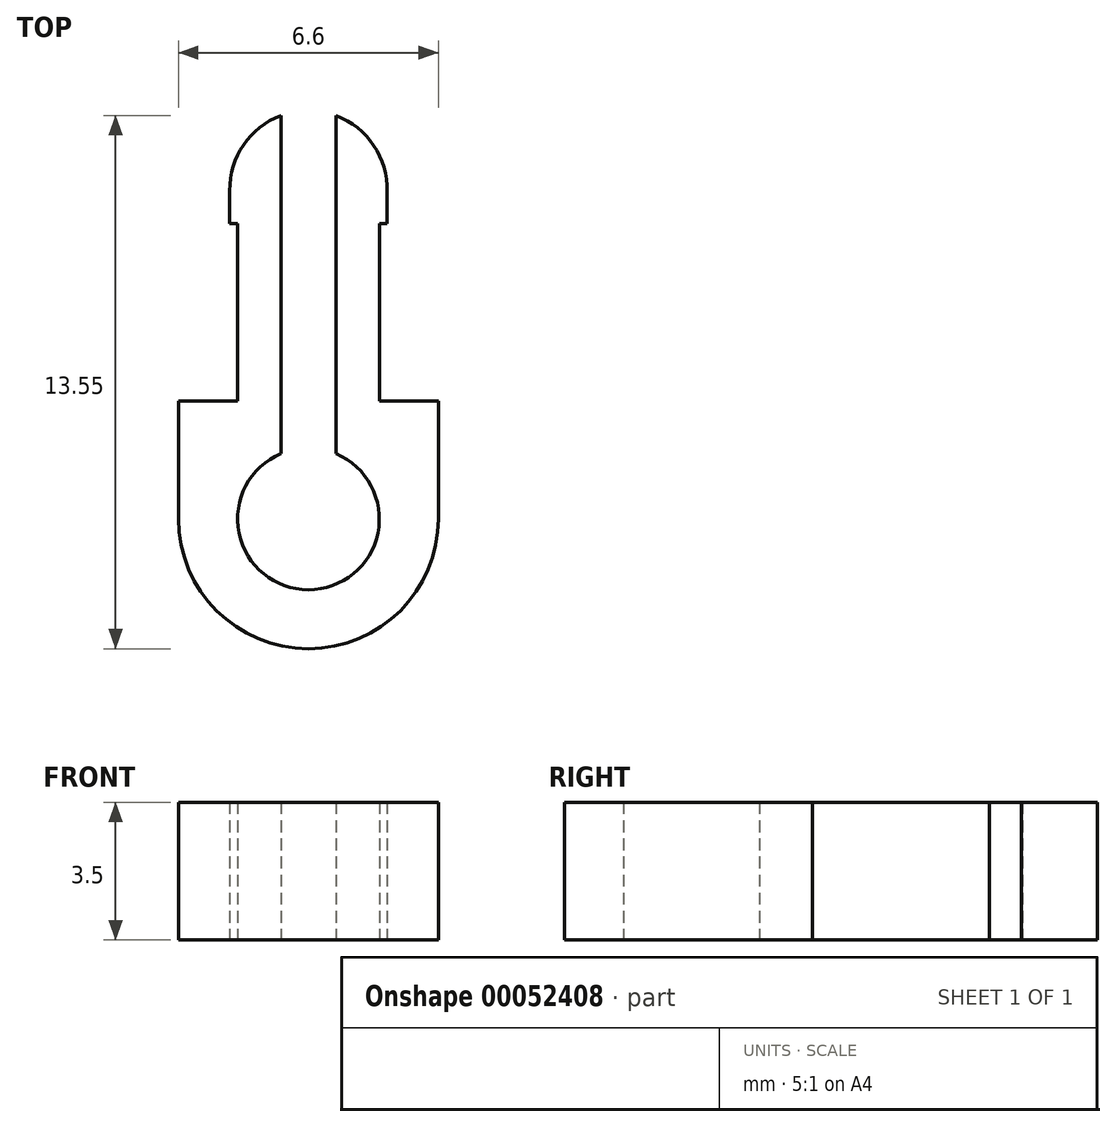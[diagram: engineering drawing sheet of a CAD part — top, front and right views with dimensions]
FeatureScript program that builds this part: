
annotation { "Feature Type Name" : "Feature", "Feature Type Description" : "" }
export const myFeature = defineFeature(function(context is Context, id is Id, definition is map)
    precondition{}
    {
        {
            var Q0;
            Q0=qCreatedBy(makeId("Top.planeOp"),FACE);
            var sketch = newSketch(context, id + "F0", { "sketchPlane" : qUnion([Q0])});
            skArc(sketch, "E0", {"start": v(-0.7, 1.66) * mm, "mid": v(0, -1.8) * mm, "end": v(0.7, 1.66) * mm});
            skArc(sketch, "E1", {"start": v(2, 8.31) * mm, "mid": v(1.66, 9.49) * mm, "end": v(0.7, 10.25) * mm});
            skArc(sketch, "E2", {"start": v(-3.3, 0) * mm, "mid": v(0, -3.3) * mm, "end": v(3.3, 0) * mm});
            skLineSegment(sketch, "E3", {"start": v(-1.8, 7.5) * mm, "end": v(-1.8, 3) * mm});
            skLineSegment(sketch, "E4", {"start": v(1.8, 7.5) * mm, "end": v(1.8, 3) * mm});
            skLineSegment(sketch, "E5", {"start": v(0.7, 10.25) * mm, "end": v(0.7, 1.66) * mm});
            skLineSegment(sketch, "E6", {"start": v(-3.3, 0) * mm, "end": v(-3.3, 3) * mm});
            skLineSegment(sketch, "E7", {"start": v(3.3, 0) * mm, "end": v(3.3, 3) * mm});
            skLineSegment(sketch, "E8.trimOffspring", {"start": v(-1.8, 3) * mm, "end": v(-3.3, 3) * mm});
            skLineSegment(sketch, "E9.trimOffspring", {"start": v(1.8, 3) * mm, "end": v(3.3, 3) * mm});
            skArc(sketch, "E10.trimOffspring", {"start": v(-0.7, 10.25) * mm, "mid": v(-1.65, 9.5) * mm, "end": v(-2, 8.34) * mm});
            skLineSegment(sketch, "E11", {"start": v(-2, 7.5) * mm, "end": v(-1.8, 7.5) * mm});
            skLineSegment(sketch, "E12", {"start": v(2, 8.43) * mm, "end": v(2, 7.5) * mm});
            skLineSegment(sketch, "E13", {"start": v(-2, 8.4) * mm, "end": v(-2, 7.5) * mm});
            skLineSegment(sketch, "E14.trimOffspring", {"start": v(1.8, 7.5) * mm, "end": v(2, 7.5) * mm});
            skLineSegment(sketch, "E15", {"start": v(-0.7, 10.25) * mm, "end": v(-0.7, 1.66) * mm});
            skSolve(sketch);
        }
        {
            var Q0;
            Q0 = qSketchRegion(id + "F0", true);
            extrude(context, id + "F1", {"entities" : qUnion([Q0]), "depth" : 3.5 * mm});
        }
    });
